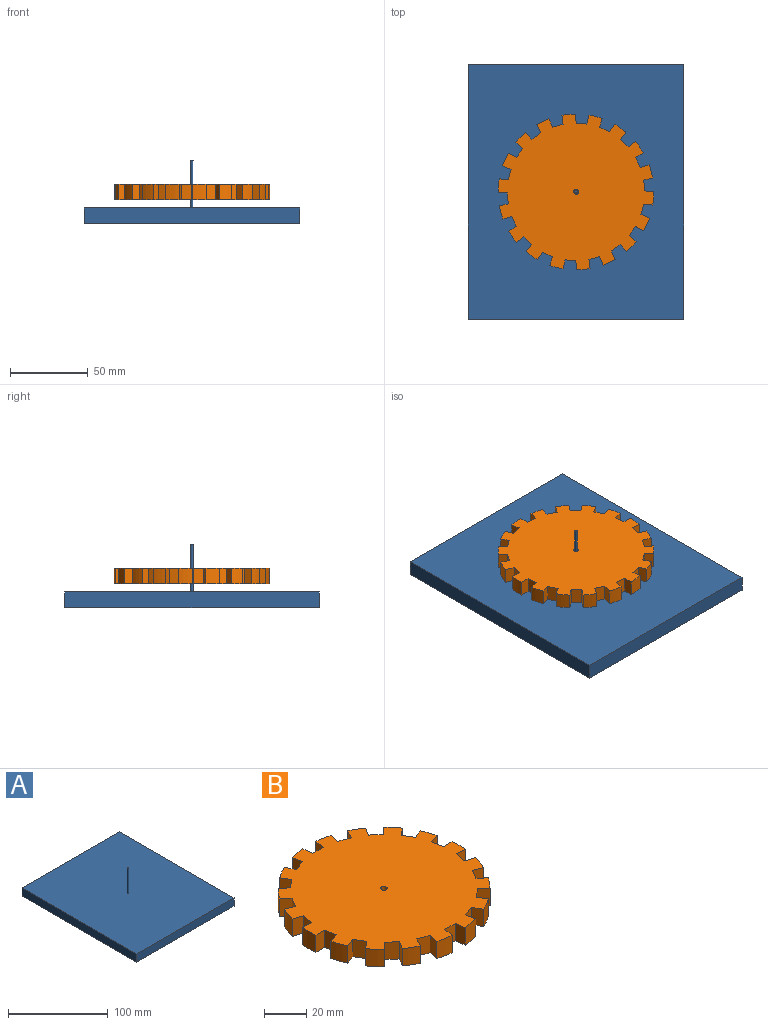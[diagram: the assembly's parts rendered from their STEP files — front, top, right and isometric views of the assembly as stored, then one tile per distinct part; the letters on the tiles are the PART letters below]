
ASSEMBLY  parts=2 mates=1
PART A: 8 faces, bbox 138.2x163x40.5 mm
  f0: cylinder r=0.91mm len=30.5mm, axis (0,0,-1), area 174.4mm2, adj f1,f7
  f1: plane 1.82x1.82mm, normal (0,0,1), area 2.6mm2, adj f0
  f2: plane 163.02x10mm, normal (-1,0,0), area 1630.2mm2, adj f3,f5,f6,f7
  f3: plane 138.19x10mm, normal (0,1,0), area 1381.9mm2, adj f2,f4,f6,f7
  f4: plane 163.02x10mm, normal (1,0,0), area 1630.2mm2, adj f3,f5,f6,f7
  f5: plane 138.19x10mm, normal (0,-1,0), area 1381.9mm2, adj f2,f4,f6,f7
  f6: plane 163.02x138.19mm, normal (0,0,-1), area 22527.5mm2, adj f2,f3,f4,f5
  f7: plane 163.02x138.19mm, normal (0,0,1), area 22524.9mm2, adj f0,f2,f3,f4,f5
PART B: 77 faces, bbox 100x99.6x11.8 mm
  f0: plane 100x99.63mm, normal (0,0,-1), area 2092.8mm2, adj f2,f3,f4,f5,f6,f7,f8,f9
  f1: plane 69.22x69.22mm, normal (0,0,-1), area 3755.8mm2, adj f19,f76
  f2: cylinder r=50mm len=10mm, axis (0,0,-1), area 88.6mm2, adj f0,f21,f23,f73
  f3: cylinder r=50mm len=10mm, axis (0,0,-1), area 88.6mm2, adj f0,f21,f72,f75
  f4: cylinder r=50mm len=10mm, axis (0,0,-1), area 88.6mm2, adj f0,f21,f69,f71
  f5: cylinder r=50mm len=10mm, axis (0,0,-1), area 88.6mm2, adj f0,f21,f66,f68
  f6: cylinder r=50mm len=10mm, axis (0,0,-1), area 88.6mm2, adj f0,f21,f63,f65
  f7: cylinder r=50mm len=10mm, axis (0,0,-1), area 88.6mm2, adj f0,f21,f60,f62
  f8: cylinder r=50mm len=10mm, axis (0,0,-1), area 88.6mm2, adj f0,f21,f57,f59
  f9: cylinder r=50mm len=10mm, axis (0,0,-1), area 88.6mm2, adj f0,f21,f54,f56
  f10: cylinder r=50mm len=10mm, axis (0,0,-1), area 88.6mm2, adj f0,f21,f51,f53
  f11: cylinder r=50mm len=10mm, axis (0,0,-1), area 88.6mm2, adj f0,f21,f48,f50
  f12: cylinder r=50mm len=10mm, axis (0,0,-1), area 88.6mm2, adj f0,f21,f45,f47
  f13: cylinder r=50mm len=10mm, axis (0,0,-1), area 88.6mm2, adj f0,f21,f42,f44
  f14: cylinder r=50mm len=10mm, axis (0,0,-1), area 88.6mm2, adj f0,f21,f39,f41
  f15: cylinder r=50mm len=10mm, axis (0,0,-1), area 88.6mm2, adj f0,f21,f36,f38
  f16: cylinder r=50mm len=10mm, axis (0,0,-1), area 88.6mm2, adj f0,f21,f33,f35
  f17: cylinder r=50mm len=10mm, axis (0,0,-1), area 88.6mm2, adj f0,f21,f30,f32
  f18: cylinder r=50mm len=10mm, axis (0,0,-1), area 88.6mm2, adj f0,f21,f27,f29
  f19: cylinder r=1.5mm len=10mm, axis (0,0,-1), area 94.2mm2, adj f1,f21
  f20: cylinder r=50mm len=10mm, axis (0,0,-1), area 88.6mm2, adj f0,f21,f24,f26
  f21: plane 100x99.63mm, normal (0,0,1), area 7014.4mm2, adj f2,f3,f4,f5,f6,f7,f8,f9
  f22: plane 10x6.83mm, normal (0.98,-0.17,0), area 69.4mm2, adj f0,f21,f23,f24
  f23: plane 10x5.88mm, normal (-0.03,-1,0), area 58.8mm2, adj f0,f2,f21,f22
  f24: plane 10x5.59mm, normal (0.31,0.95,0), area 58.8mm2, adj f0,f20,f21,f22
  f25: plane 10x6.01mm, normal (0.87,-0.5,0), area 69.4mm2, adj f0,f21,f26,f27
  f26: plane 10x5.46mm, normal (-0.37,-0.93,0), area 58.8mm2, adj f0,f20,f21,f25
  f27: plane 10x4.63mm, normal (0.62,0.79,0), area 58.8mm2, adj f0,f18,f21,f25
  f28: plane 10x5.31mm, normal (0.64,-0.77,0), area 69.4mm2, adj f0,f21,f29,f30
  f29: plane 10x4.38mm, normal (-0.67,-0.74,0), area 58.8mm2, adj f0,f18,f21,f28
  f30: plane 10x4.99mm, normal (0.85,0.53,0), area 58.8mm2, adj f0,f17,f21,f28
  f31: plane 10x6.52mm, normal (0.34,-0.94,0), area 69.4mm2, adj f0,f21,f32,f33
  f32: plane 10x5.19mm, normal (-0.88,-0.47,0), area 58.8mm2, adj f0,f17,f21,f31
  f33: plane 10x5.75mm, normal (0.98,0.21,0), area 58.8mm2, adj f0,f16,f21,f31
  f34: plane 10x6.94mm, normal (0,-1,0), area 69.4mm2, adj f0,f21,f35,f36
  f35: plane 10x5.82mm, normal (-0.99,-0.14,0), area 58.8mm2, adj f0,f16,f21,f34
  f36: plane 10x5.82mm, normal (0.99,-0.14,0), area 58.8mm2, adj f0,f15,f21,f34
  f37: plane 10x6.52mm, normal (-0.34,-0.94,0), area 69.4mm2, adj f0,f21,f38,f39
  f38: plane 10x5.75mm, normal (-0.98,0.21,0), area 58.8mm2, adj f0,f15,f21,f37
  f39: plane 10x5.19mm, normal (0.88,-0.47,0), area 58.8mm2, adj f0,f14,f21,f37
  f40: plane 10x5.31mm, normal (-0.64,-0.77,0), area 69.4mm2, adj f0,f21,f41,f42
  f41: plane 10x4.99mm, normal (-0.85,0.53,0), area 58.8mm2, adj f0,f14,f21,f40
  f42: plane 10x4.38mm, normal (0.67,-0.74,0), area 58.8mm2, adj f0,f13,f21,f40
  f43: plane 10x6.01mm, normal (-0.87,-0.5,0), area 69.4mm2, adj f0,f21,f44,f45
  f44: plane 10x4.63mm, normal (-0.62,0.79,0), area 58.8mm2, adj f0,f13,f21,f43
  f45: plane 10x5.46mm, normal (0.37,-0.93,0), area 58.8mm2, adj f0,f12,f21,f43
  f46: plane 10x6.83mm, normal (-0.98,-0.17,0), area 69.4mm2, adj f0,f21,f47,f48
  f47: plane 10x5.59mm, normal (-0.31,0.95,0), area 58.8mm2, adj f0,f12,f21,f46
  f48: plane 10x5.88mm, normal (0.03,-1,0), area 58.8mm2, adj f0,f11,f21,f46
  f49: plane 10x6.83mm, normal (-0.98,0.17,0), area 69.4mm2, adj f0,f21,f50,f51
  f50: plane 10x5.88mm, normal (0.03,1,0), area 58.8mm2, adj f0,f11,f21,f49
  f51: plane 10x5.59mm, normal (-0.31,-0.95,0), area 58.8mm2, adj f0,f10,f21,f49
  f52: plane 10x6.01mm, normal (-0.87,0.5,0), area 69.4mm2, adj f0,f21,f53,f54
  f53: plane 10x5.46mm, normal (0.37,0.93,0), area 58.8mm2, adj f0,f10,f21,f52
  f54: plane 10x4.63mm, normal (-0.62,-0.79,0), area 58.8mm2, adj f0,f9,f21,f52
  f55: plane 10x5.31mm, normal (-0.64,0.77,0), area 69.4mm2, adj f0,f21,f56,f57
  f56: plane 10x4.38mm, normal (0.67,0.74,0), area 58.8mm2, adj f0,f9,f21,f55
  f57: plane 10x4.99mm, normal (-0.85,-0.53,0), area 58.8mm2, adj f0,f8,f21,f55
  f58: plane 10x6.52mm, normal (-0.34,0.94,0), area 69.4mm2, adj f0,f21,f59,f60
  f59: plane 10x5.19mm, normal (0.88,0.47,0), area 58.8mm2, adj f0,f8,f21,f58
  f60: plane 10x5.75mm, normal (-0.98,-0.21,0), area 58.8mm2, adj f0,f7,f21,f58
  f61: plane 10x6.94mm, normal (0,1,0), area 69.4mm2, adj f0,f21,f62,f63
  f62: plane 10x5.82mm, normal (0.99,0.14,0), area 58.8mm2, adj f0,f7,f21,f61
  f63: plane 10x5.82mm, normal (-0.99,0.14,0), area 58.8mm2, adj f0,f6,f21,f61
  f64: plane 10x6.52mm, normal (0.34,0.94,0), area 69.4mm2, adj f0,f21,f65,f66
  f65: plane 10x5.75mm, normal (0.98,-0.21,0), area 58.8mm2, adj f0,f6,f21,f64
  f66: plane 10x5.19mm, normal (-0.88,0.47,0), area 58.8mm2, adj f0,f5,f21,f64
  f67: plane 10x5.31mm, normal (0.64,0.77,0), area 69.4mm2, adj f0,f21,f68,f69
  f68: plane 10x4.99mm, normal (0.85,-0.53,0), area 58.8mm2, adj f0,f5,f21,f67
  f69: plane 10x4.38mm, normal (-0.67,0.74,0), area 58.8mm2, adj f0,f4,f21,f67
  f70: plane 10x6.01mm, normal (0.87,0.5,0), area 69.4mm2, adj f0,f21,f71,f72
  f71: plane 10x4.63mm, normal (0.62,-0.79,0), area 58.8mm2, adj f0,f4,f21,f70
  f72: plane 10x5.46mm, normal (-0.37,0.93,0), area 58.8mm2, adj f0,f3,f21,f70
  f73: plane 10x5.88mm, normal (-0.03,1,0), area 58.8mm2, adj f0,f2,f21,f74
  f74: plane 10x6.83mm, normal (0.98,0.17,0), area 69.4mm2, adj f0,f21,f73,f75
  f75: plane 10x5.59mm, normal (0.31,-0.95,0), area 58.8mm2, adj f0,f3,f21,f74
  f76: torus R=37.11mm, axis (0,0,-1), area 1831.2mm2, adj f0,f1
PLACE A t=(-4.12,9.71,8.39)mm fixed
PLACE B rot(axis=(0,0,1),155.4deg) t=(-4.12,9.71,13.14)mm
MATE revolute B.f19 <-> A.f0  axis (0,0,1) through (-4.12,9.71,23.14)mm
